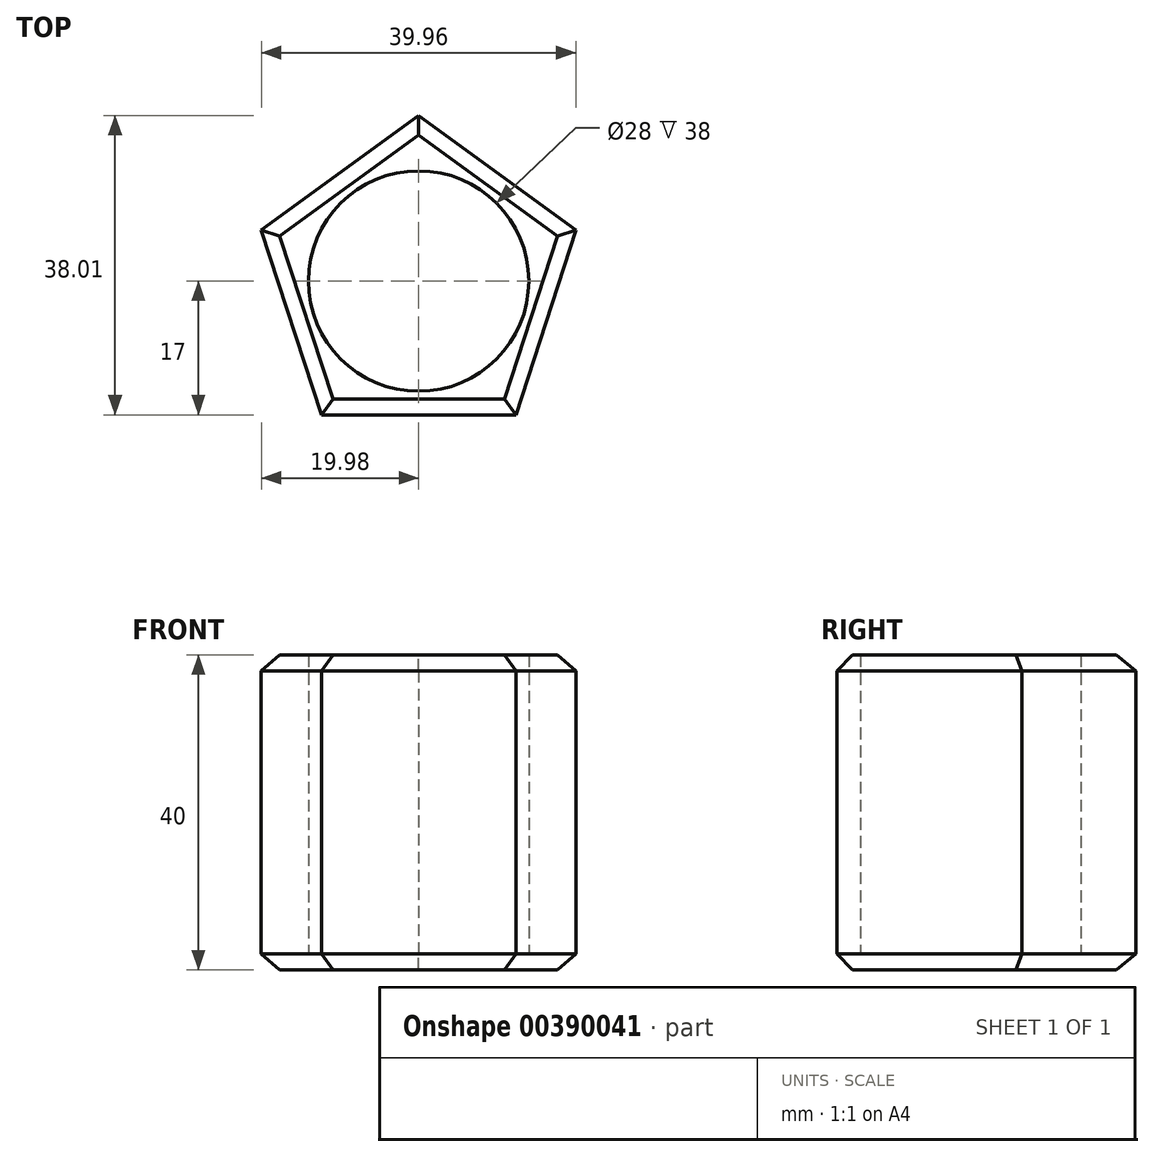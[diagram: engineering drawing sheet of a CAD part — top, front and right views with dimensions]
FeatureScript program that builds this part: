
annotation { "Feature Type Name" : "Feature", "Feature Type Description" : "" }
export const myFeature = defineFeature(function(context is Context, id is Id, definition is map)
    precondition{}
    {
        {
            var Q0;
            Q0=qCreatedBy(makeId("Top.planeOp"),FACE);
            var sketch = newSketch(context, id + "F0", { "sketchPlane" : qUnion([Q0])});
            skCircle(sketch, "E0", {"center": v(0, 0) * mm, "radius": 14 * mm});
            skCircle(sketch, "E1.cCircle", {"center": v(0, 0) * mm, "radius": 17 * mm, "construction": true});
            skLineSegment(sketch, "E1.0", {"start": v(19.98, 6.5) * mm, "end": v(12.35, -17) * mm});
            skLineSegment(sketch, "E1.1", {"start": v(12.35, -17) * mm, "end": v(-12.35, -17) * mm});
            skLineSegment(sketch, "E1.2", {"start": v(-12.35, -17) * mm, "end": v(-19.98, 6.5) * mm});
            skLineSegment(sketch, "E1.3", {"start": v(-19.98, 6.5) * mm, "end": v(0, 21.01) * mm});
            skLineSegment(sketch, "E1.4", {"start": v(0, 21.01) * mm, "end": v(19.98, 6.5) * mm});
            skPoint(sketch, "E1.0.midPoint", {"position": v(16.17, -5.25) * mm});
            skPoint(sketch, "E2", {"position": v(0, -14) * mm});
            skSolve(sketch);
        }
        {
            var Q0;
            Q0 = qSketchRegion(id + "F0", true);
            var Q1;
            Q1=makeQuery(id+"F0.imprint","IMPRINT",FACE,{"disambiguationData":[TD([[makeQuery(id+"F0.imprint","IMPRINT",EDGE,{"derivedFrom":sQuery(id+"F0.wireOp",EDGE,"E0")}),1.0]])]});
            extrude(context, id + "F1", {"entities" : qUnion([Q0, Q1]), "depth" : 2 * mm});
        }
        {
            var Q0;
            Q0 = qSketchRegion(id + "F0", true);
            extrude(context, id + "F2", {"entities" : qUnion([Q0]), "operationType" : NewBodyOperationType.ADD, "depth" : 40 * mm});
        }
        {
            var Q0;
            Q0=makeQuery(id+"F2.opExtrude","CAP_EDGE",EDGE,{"disambiguationData":[OSD([sQuery(id+"F0.wireOp",EDGE,"E1.0")])],"isStart":false});
            var Q1;
            Q1=makeQuery(id+"F2.opExtrude","CAP_EDGE",EDGE,{"disambiguationData":[OSD([sQuery(id+"F0.wireOp",EDGE,"E1.4")])],"isStart":false});
            var Q2;
            Q2=makeQuery(id+"F2.opExtrude","CAP_EDGE",EDGE,{"disambiguationData":[OSD([sQuery(id+"F0.wireOp",EDGE,"E1.3")])],"isStart":false});
            var Q3;
            Q3=makeQuery(id+"F2.opExtrude","CAP_EDGE",EDGE,{"disambiguationData":[OSD([sQuery(id+"F0.wireOp",EDGE,"E1.2")])],"isStart":false});
            var Q4;
            Q4=makeQuery(id+"F2.opExtrude","CAP_EDGE",EDGE,{"disambiguationData":[OSD([sQuery(id+"F0.wireOp",EDGE,"E1.1")])],"isStart":false});
            var Q5;
            Q5=makeQuery(id+"F1.opExtrude","CAP_EDGE",EDGE,{"disambiguationData":[OSD([sQuery(id+"F0.wireOp",EDGE,"E1.0")])],"isStart":true});
            var Q6;
            Q6=makeQuery(id+"F1.opExtrude","CAP_EDGE",EDGE,{"disambiguationData":[OSD([sQuery(id+"F0.wireOp",EDGE,"E1.4")])],"isStart":true});
            var Q7;
            Q7=makeQuery(id+"F1.opExtrude","CAP_FACE",FACE,{"disambiguationData":[OSD([sQuery(id+"F0.wireOp",EDGE,"E1.0"),sQuery(id+"F0.wireOp",EDGE,"E1.1"),sQuery(id+"F0.wireOp",EDGE,"E1.2"),sQuery(id+"F0.wireOp",EDGE,"E1.3"),sQuery(id+"F0.wireOp",EDGE,"E1.4")])],"isStart":true});
            chamfer(context, id + "F3", {"entities" : qUnion([Q0, Q1, Q2, Q3, Q4, Q5, Q6, Q7]), "width" : 2 * mm, "tangentPropagation" : true});
        }
    });
